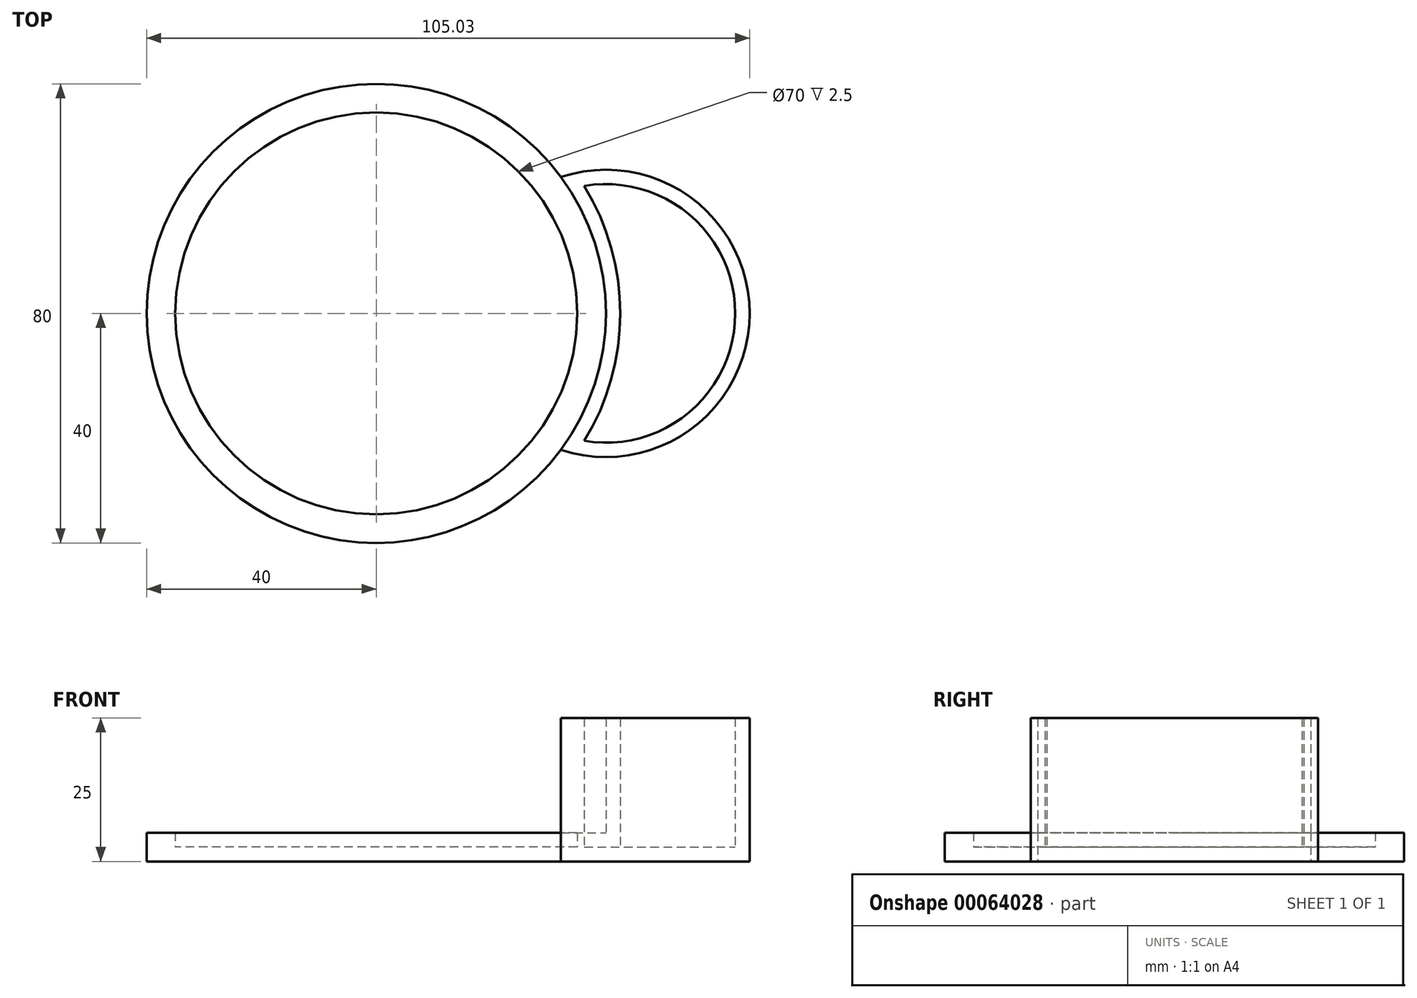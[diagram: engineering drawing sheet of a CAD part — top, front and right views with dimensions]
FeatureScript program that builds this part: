
annotation { "Feature Type Name" : "Feature", "Feature Type Description" : "" }
export const myFeature = defineFeature(function(context is Context, id is Id, definition is map)
    precondition{}
    {
        {
            var Q0;
            Q0=qCreatedBy(makeId("Top.planeOp"),FACE);
            var sketch = newSketch(context, id + "F0", { "sketchPlane" : qUnion([Q0])});
            skCircle(sketch, "E0", {"center": v(0, 0) * mm, "radius": 40 * mm});
            skArc(sketch, "E1", {"start": v(32.17, -23.77) * mm, "mid": v(65.03, 0) * mm, "end": v(32.17, 23.77) * mm});
            skCircle(sketch, "E2.0", {"center": v(0, 0) * mm, "radius": 35 * mm});
            skArc(sketch, "E3", {"start": v(32.17, -23.77) * mm, "mid": v(40, 0) * mm, "end": v(32.17, 23.77) * mm});
            skArc(sketch, "E4.0", {"start": v(36.23, -22.21) * mm, "mid": v(42.5, 0) * mm, "end": v(36.23, 22.21) * mm});
            skArc(sketch, "E4.1", {"start": v(36.23, -22.21) * mm, "mid": v(62.53, 0) * mm, "end": v(36.23, 22.21) * mm});
            skSolve(sketch);
        }
        {
            var Q0;
            {var subQ0=sQuery(id+"F0.wireOp",EDGE,"E1");Q0=makeQuery(id+"F0.imprint","IMPRINT",FACE,{"disambiguationData":[TD([[makeQuery(id+"F0.imprint","IMPRINT",EDGE,{"derivedFrom":subQ0}),1.0]])]});}
            extrude(context, id + "F1", {"entities" : qUnion([Q0]), "depth" : 25 * mm});
        }
        {
            var Q0;
            Q0=makeQuery(id+"F0.imprint","IMPRINT",FACE,{"disambiguationData":[TD([[makeQuery(id+"F0.imprint","IMPRINT",EDGE,{"derivedFrom":sQuery(id+"F0.wireOp",EDGE,"E2.0")}),-1.0]])]});
            extrude(context, id + "F2", {"entities" : qUnion([Q0]), "operationType" : NewBodyOperationType.ADD, "depth" : 5 * mm});
        }
        {
            var Q0;
            Q0=makeQuery(id+"F0.imprint","IMPRINT",FACE,{"disambiguationData":[TD([[makeQuery(id+"F0.imprint","IMPRINT",EDGE,{"derivedFrom":sQuery(id+"F0.wireOp",EDGE,"E2.0")}),1.0]])]});
            extrude(context, id + "F3", {"entities" : qUnion([Q0]), "operationType" : NewBodyOperationType.ADD, "depth" : 2.5 * mm});
        }
        {
            var Q0;
            Q0=makeQuery(id+"F0.imprint","IMPRINT",FACE,{"disambiguationData":[TD([[makeQuery(id+"F0.imprint","IMPRINT",EDGE,{"derivedFrom":sQuery(id+"F0.wireOp",EDGE,"E4.0")}),-1.0]])]});
            extrude(context, id + "F4", {"entities" : qUnion([Q0]), "operationType" : NewBodyOperationType.ADD, "depth" : 2.5 * mm});
        }
    });
